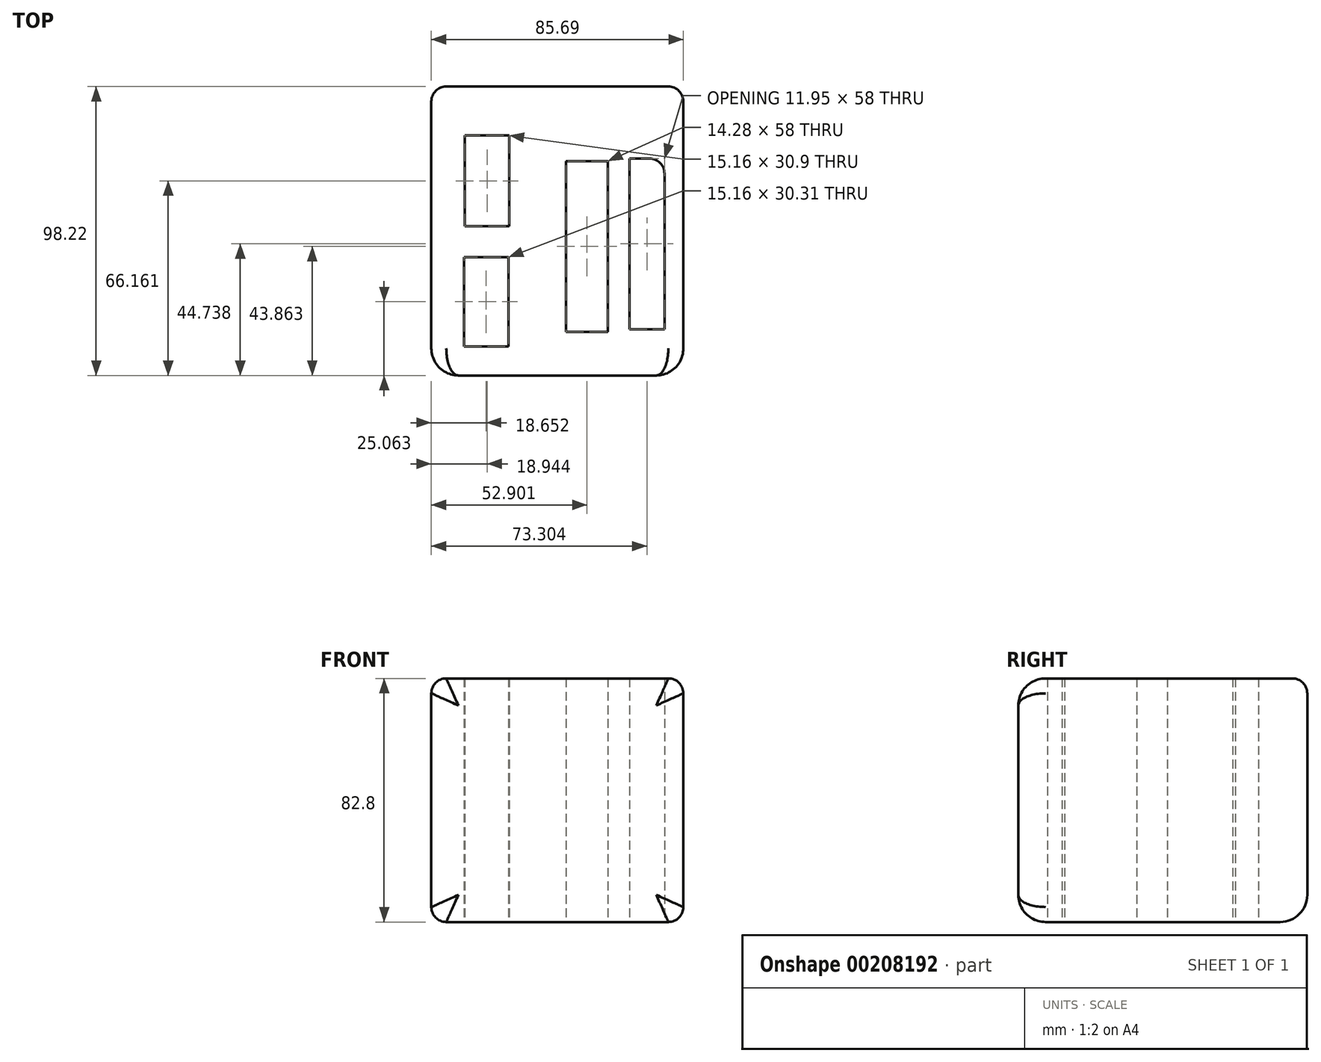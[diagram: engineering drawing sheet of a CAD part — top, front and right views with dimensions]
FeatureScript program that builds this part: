
annotation { "Feature Type Name" : "Feature", "Feature Type Description" : "" }
export const myFeature = defineFeature(function(context is Context, id is Id, definition is map)
    precondition{}
    {
        {
            var Q0;
            Q0=qCreatedBy(makeId("Top.planeOp"),FACE);
            var sketch = newSketch(context, id + "F0", { "sketchPlane" : qUnion([Q0])});
            skLineSegment(sketch, "E0.bottom", {"start": v(-40.95, -40.22) * mm, "end": v(44.74, -40.22) * mm});
            skLineSegment(sketch, "E0.top", {"start": v(-40.95, 58) * mm, "end": v(44.74, 58) * mm});
            skLineSegment(sketch, "E0.left", {"start": v(-40.95, -40.22) * mm, "end": v(-40.95, 58) * mm});
            skLineSegment(sketch, "E0.right", {"start": v(44.74, -40.22) * mm, "end": v(44.74, 58) * mm});
            skLineSegment(sketch, "E1.bottom", {"start": v(-29.88, -30.31) * mm, "end": v(-14.72, -30.31) * mm});
            skLineSegment(sketch, "E1.top", {"start": v(-29.88, 0) * mm, "end": v(-14.72, 0) * mm});
            skLineSegment(sketch, "E1.left", {"start": v(-29.88, -30.31) * mm, "end": v(-29.88, 0) * mm});
            skLineSegment(sketch, "E1.right", {"start": v(-14.72, -30.31) * mm, "end": v(-14.72, 0) * mm});
            skLineSegment(sketch, "E2.bottom", {"start": v(-29.58, 10.5) * mm, "end": v(-14.43, 10.5) * mm});
            skLineSegment(sketch, "E2.top", {"start": v(-29.58, 41.39) * mm, "end": v(-14.43, 41.39) * mm});
            skLineSegment(sketch, "E2.left", {"start": v(-29.58, 10.5) * mm, "end": v(-29.58, 41.39) * mm});
            skLineSegment(sketch, "E2.right", {"start": v(-14.43, 10.5) * mm, "end": v(-14.43, 41.39) * mm});
            skLineSegment(sketch, "E3.bottom", {"start": v(4.8, -25.36) * mm, "end": v(19.1, -25.36) * mm});
            skLineSegment(sketch, "E3.top", {"start": v(4.8, 32.65) * mm, "end": v(19.1, 32.65) * mm});
            skLineSegment(sketch, "E3.left", {"start": v(4.8, -25.36) * mm, "end": v(4.8, 32.65) * mm});
            skLineSegment(sketch, "E3.right", {"start": v(19.1, -25.36) * mm, "end": v(19.1, 32.65) * mm});
            skLineSegment(sketch, "E4.bottom", {"start": v(26.38, -24.48) * mm, "end": v(38.33, -24.48) * mm});
            skLineSegment(sketch, "E4.top", {"start": v(26.38, 33.52) * mm, "end": v(38.33, 33.52) * mm});
            skLineSegment(sketch, "E4.left", {"start": v(26.38, -24.48) * mm, "end": v(26.38, 33.52) * mm});
            skLineSegment(sketch, "E4.right", {"start": v(38.33, -24.48) * mm, "end": v(38.33, 33.52) * mm});
            skSolve(sketch);
        }
        {
            var Q0;
            Q0 = qSketchRegion(id + "F0", true);
            extrude(context, id + "F1", {"entities" : qUnion([Q0]), "depth" : 82.8 * mm});
        }
        {
            var Q0;
            Q0=makeQuery(id+"F1.opExtrude","CAP_EDGE",EDGE,{"disambiguationData":[OSD([sQuery(id+"F0.wireOp",EDGE,"E0.top")])],"isStart":false});
            var Q1;
            Q1=makeQuery(id+"F1.opExtrude","SWEPT_EDGE",EDGE,{"disambiguationData":[OSD([sQuery(id+"F0.wireOp",EDGE,"E4.top"),sQuery(id+"F0.wireOp",EDGE,"E4.right")])]});
            fillet(context, id + "F2", {"entities" : qUnion([Q0, Q1]), "radius" : 5.08 * mm, "tangentPropagation" : true, "allowEdgeOverflow" : false});
        }
        {
            var Q0;
            Q0=makeQuery(id+"F1.opExtrude","SWEPT_FACE",FACE,{"disambiguationData":[OSD([sQuery(id+"F0.wireOp",EDGE,"E0.bottom")])]});
            var Q1;
            Q1=makeQuery(id+"F1.opExtrude","CAP_EDGE",EDGE,{"disambiguationData":[OSD([sQuery(id+"F0.wireOp",EDGE,"E0.top")])],"isStart":true});
            fillet(context, id + "F3", {"entities" : qUnion([Q0, Q1]), "radius" : 9.2 * mm, "tangentPropagation" : true, "allowEdgeOverflow" : false});
        }
        {
            var Q0;
            Q0=makeQuery(id+"F3.opFillet","BLEND_FACE",FACE,{"disambiguationData":[OSD([sQuery(id+"F0.wireOp",EDGE,"E0.top")])]});
            fillet(context, id + "F4", {"entities" : qUnion([Q0]), "radius" : 5.08 * mm, "tangentPropagation" : true, "allowEdgeOverflow" : false});
        }
    });
